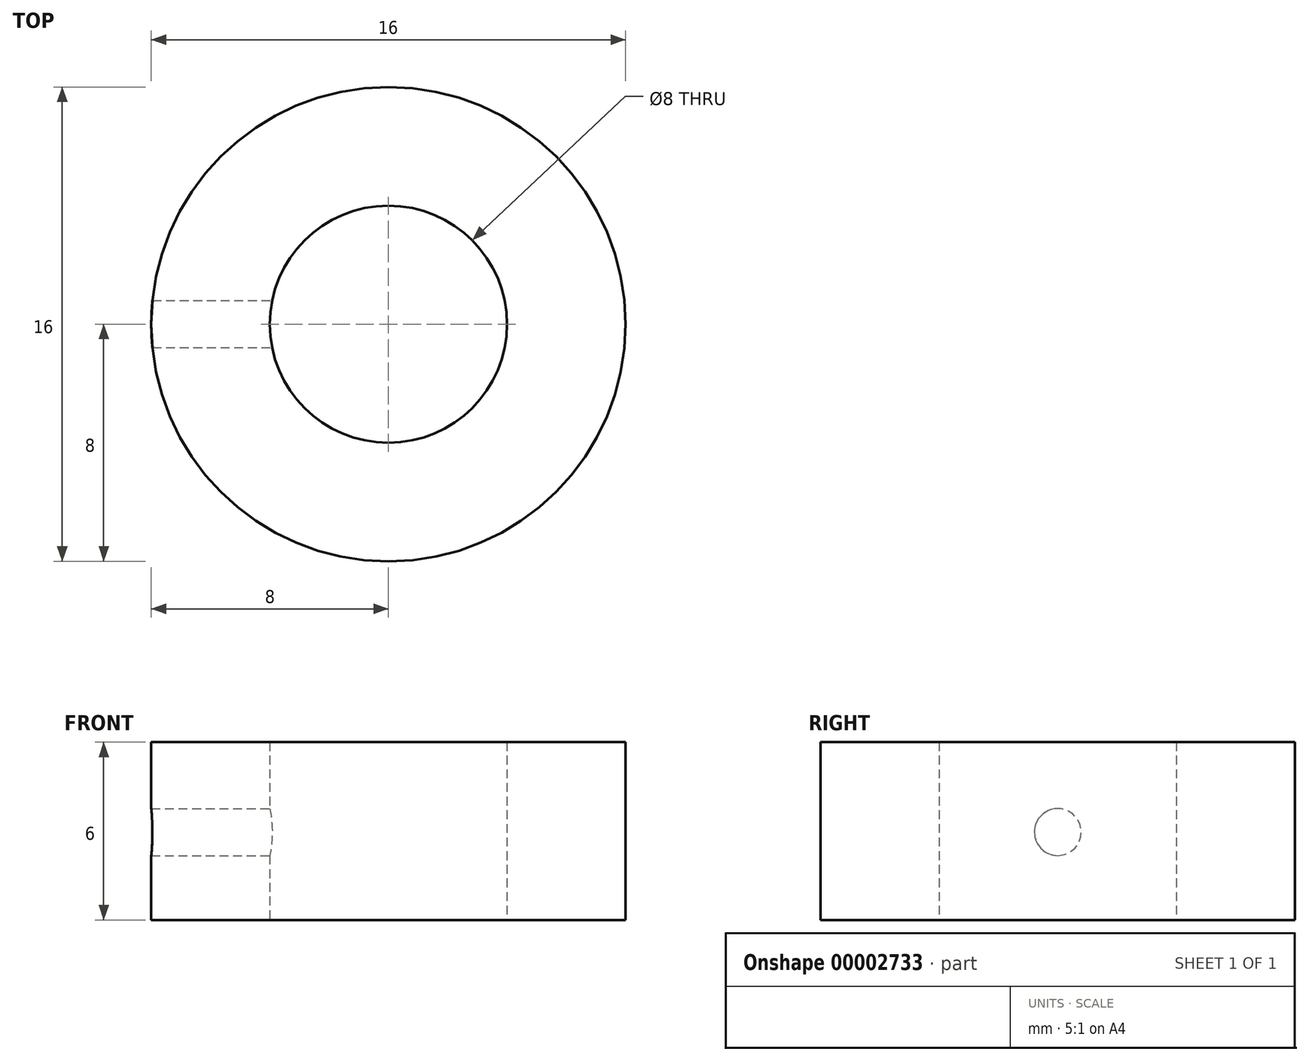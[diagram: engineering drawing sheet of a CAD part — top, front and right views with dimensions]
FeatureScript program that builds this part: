
annotation { "Feature Type Name" : "Feature", "Feature Type Description" : "" }
export const myFeature = defineFeature(function(context is Context, id is Id, definition is map)
    precondition{}
    {
        {
            var Q0;
            Q0=qCreatedBy(makeId("Top.planeOp"),FACE);
            var sketch = newSketch(context, id + "F0", { "sketchPlane" : qUnion([Q0])});
            skCircle(sketch, "E0", {"center": v(0, 0) * mm, "radius": 4 * mm});
            skCircle(sketch, "E1", {"center": v(0, 0) * mm, "radius": 8 * mm});
            skSolve(sketch);
        }
        {
            var Q0;
            Q0=makeQuery(id+"F0.imprint","IMPRINT",FACE,{"disambiguationData":[TD([[makeQuery(id+"F0.imprint","IMPRINT",EDGE,{"derivedFrom":sQuery(id+"F0.wireOp",EDGE,"E0")}),-1.0]])]});
            extrude(context, id + "F1", {"entities" : qUnion([Q0]), "depth" : 6 * mm});
        }
        {
            var Q0;
            Q0=qCreatedBy(makeId("Right.planeOp"),FACE);
            var sketch = newSketch(context, id + "F2", { "sketchPlane" : qUnion([Q0])});
            skCircle(sketch, "E2", {"center": v(0, 2.96) * mm, "radius": 0.8 * mm});
            skSolve(sketch);
        }
        {
            var Q0;
            Q0=makeQuery(id+"F2.imprint","IMPRINT",FACE,{"disambiguationData":[TD([[makeQuery(id+"F2.imprint","IMPRINT",EDGE,{"derivedFrom":sQuery(id+"F2.wireOp",EDGE,"E2")}),1.0]])]});
            extrude(context, id + "F3", {"entities" : qUnion([Q0]), "operationType" : NewBodyOperationType.REMOVE, "oppositeDirection" : true, "depth" : 8 * mm});
        }
    });
